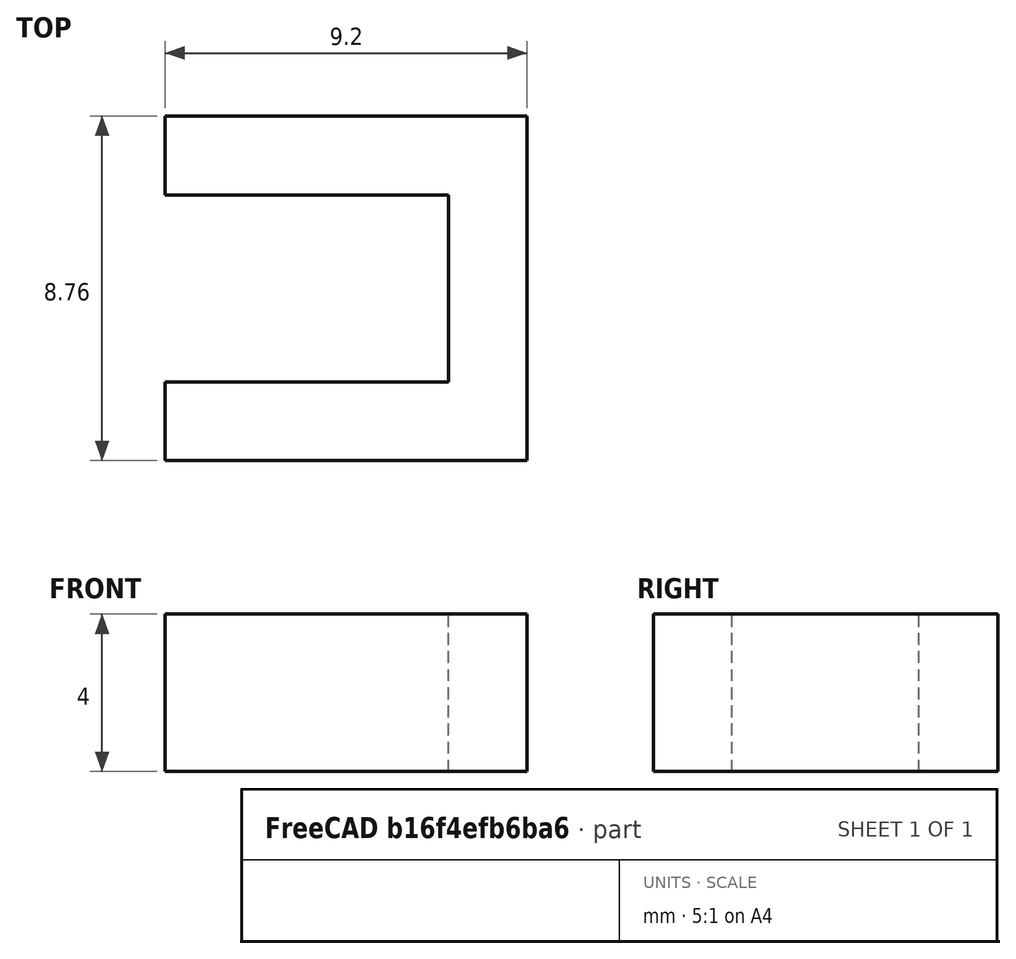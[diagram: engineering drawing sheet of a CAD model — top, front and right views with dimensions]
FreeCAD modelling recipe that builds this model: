
FCSTD DOCUMENT  (FreeCAD 0.16R4928 (Git))
Label: sujetador_w_s_h_vertial
License: CreativeCommons Attribution-ShareAlike
LicenseURL: http://creativecommons.org/licenses/by-sa/4.0/
objects: Sketcher::SketchObject×1, PartDesign::Pad×1
note: 3 computed .brp shape members not serialized (recipe doc carries the construction recipe); baked Part::Feature solids carry a one-line shape summary decoded from their .brp

FEATURE [Sketcher::SketchObject] Sketch
  sketch-geometry (8):
    g0: LineSegment StartX=-7.2 StartY=4.375 StartZ=0 EndX=2 EndY=4.375 EndZ=0
    g1: LineSegment StartX=2 StartY=4.375 StartZ=0 EndX=2 EndY=-4.375 EndZ=0
    g2: LineSegment StartX=2 StartY=-4.375 StartZ=0 EndX=-7.2 EndY=-4.375 EndZ=0
    g3: LineSegment StartX=-7.2 StartY=-4.375 StartZ=0 EndX=-7.2 EndY=-2.375 EndZ=0
    g4: LineSegment StartX=-7.2 StartY=-2.375 StartZ=0 EndX=0 EndY=-2.375 EndZ=0
    g5: LineSegment StartX=0 StartY=-2.375 StartZ=0 EndX=0 EndY=2.375 EndZ=0
    g6: LineSegment StartX=0 StartY=2.375 StartZ=0 EndX=-7.2 EndY=2.375 EndZ=0
    g7: LineSegment StartX=-7.2 StartY=2.375 StartZ=0 EndX=-7.2 EndY=4.375 EndZ=0
  constraints (24):
    c: Horizontal(g0)
    c: Coincident(g0,g1)
    c: Coincident(g1,g2)
    c: Horizontal(g2)
    c: Coincident(g2,g3)
    c: Vertical(g3)
    c: Coincident(g3,g4)
    c: Coincident(g4,g5)
    c: Vertical(g5)
    c: Coincident(g5,g6)
    c: Coincident(g6,g7)
    c: Coincident(g7,g0)
    c: Vertical(g7)
    c: Vertical(g1)
    c: Horizontal(g4)
    c: Horizontal(g6)
    c: Symmetric(g0,g1,g-1)
    c: Equal(g7,g3)
    c: Equal(g0,g2)
    c: DistanceX(g0) = 9.2
    c: Symmetric(g4,g5,g-1)
    c: DistanceX(g5,g0) = 2
    c: DistanceY(g7) = 2
    c: DistanceY(g5) = 4.75
FEATURE [PartDesign::Pad] Pad
  Length = 4
  Length2 = 100
  Midplane = true
  Sketch = -> Sketch
  Type = 0
